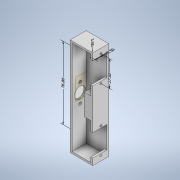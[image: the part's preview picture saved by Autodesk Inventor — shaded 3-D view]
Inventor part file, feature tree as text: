
AUTODESK INVENTOR PART (.ipt)
format: ipt  version: 2022.2 (Build 262287010, 287A)  size: 248,320 bytes
history: native  units: mm
features: extrude x11, sketch x10, other x6
ambient origin geometry x8: Origin, YZ Plane, XZ Plane, XY Plane, X Axis, Y Axis, Z Axis, Center Point
bodies: Solid1 (feature_tree)
feature tree (27):
  other  "Annotations"
  extrude  "Extrusion1"  Depth=100.0mm
  extrude  "Extrusion2"  Depth=2.0mm
  extrude  "Extrusion3"  Depth=15.0mm TaperAngle=0.0deg
  extrude  "Extrusion4"  Depth=2.0mm
  extrude  "Extrusion5"  Depth=8.5mm
  extrude  "Extrusion12"  Depth=3.0mm
  extrude  "Extrusion13"  Depth=23.5mm
  extrude  "Extrusion14"  Depth=5.0mm
  extrude  "Extrusion15"  Depth=5.0mm
  other  "Plano de trabalho3"
  extrude  "Extrusion18"  Depth=2.0mm TaperAngle=0.0deg
  extrude  "Extrusão19"  Depth=15.0mm
  sketch  "Sketch1"  dims[d0=24.0mm d1=100.0mm]
  sketch  "Sketch2"  dims[d2=2.0mm d3=0.0mm d4=2.0mm]
  sketch  "Sketch3"  dims[d5=2.0mm d6=15.0mm d7=0.0mm]
  sketch  "Sketch5"  dims[d8=2.0mm d9=2.0mm]
  sketch  "Sketch15"  dims[d10=8.5mm d11=8.5mm]
  sketch  "Sketch16"  dims[d12=27.5mm d13=3.0mm]
  sketch  "Sketch17"  dims[d14=12.0mm d15=0.0mm d24=23.5mm]
  sketch  "Sketch18"  dims[d27=15.0mm d28=0.0mm d29=5.0mm]
  sketch  "Sketch21"  dims[d30=5.0mm d31=0.0mm d32=8.6mm]
  sketch  "Esboço22"  dims[d33=0.0mm d70=2.0mm d71=0.0mm d84=15.0mm d85=23.5mm d86=5.0mm d87=2.0mm d88=2.0mm d89=8.5mm d90=8.5mm d91=2.0mm d92=2.0mm d93=2.0mm d94=0.0mm d95=2.0mm d96=0.0mm d97=5.0mm d98=13.6mm d99=8.5mm d100=5.0mm d101=0.0mm d104=15.0mm d105=2.0mm d106=2.0mm d122=12.0mm d124=8.5mm d125=10.0mm d126=0.0mm d129=3.0mm d130=3.0mm d131=10.0mm d132=10.0mm d134=50.0mm d142=7.0mm d143=10.0mm d144=10.0mm d145=10.0mm d146=0.0mm d110=76.8mm d78=4.776933mm d79=3.0mm d80=27.5mm d81=7.865088mm d82=1.505127mm d83=8.5mm]
  other  "Linear Dimension 6"
  other  "Linear Dimension 7"
  other  "Linear Dimension 8"
  other  "Linear Dimension 10"
